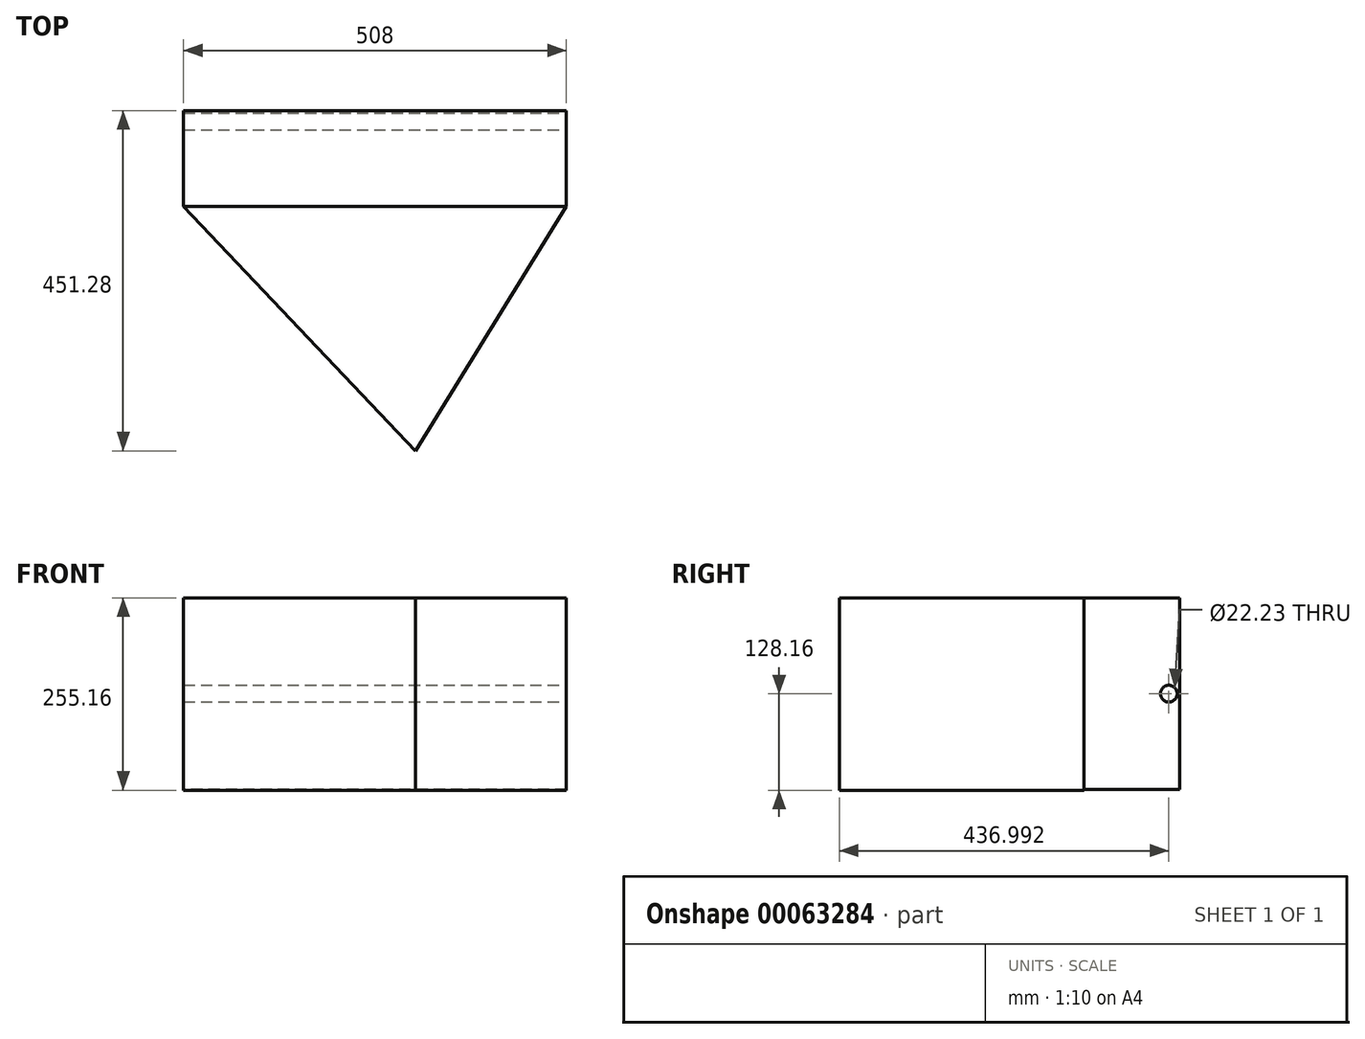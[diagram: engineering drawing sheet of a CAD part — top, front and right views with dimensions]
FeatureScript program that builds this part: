
annotation { "Feature Type Name" : "Feature", "Feature Type Description" : "" }
export const myFeature = defineFeature(function(context is Context, id is Id, definition is map)
    precondition{}
    {
        {
            var Q0;
            Q0=qCreatedBy(makeId("Front.planeOp"),FACE);
            var sketch = newSketch(context, id + "F0", { "sketchPlane" : qUnion([Q0])});
            skLineSegment(sketch, "E0.rect.bottom", {"start": v(254, 127) * mm, "end": v(-254, 127) * mm});
            skLineSegment(sketch, "E0.rect.top", {"start": v(254, -127) * mm, "end": v(-254, -127) * mm});
            skLineSegment(sketch, "E0.rect.left", {"start": v(254, 127) * mm, "end": v(254, -127) * mm});
            skLineSegment(sketch, "E0.rect.right", {"start": v(-254, 127) * mm, "end": v(-254, -127) * mm});
            skPoint(sketch, "E0.rect.middle", {"position": v(0, 0) * mm});
            skSolve(sketch);
        }
        {
            var Q0;
            Q0 = qSketchRegion(id + "F0", true);
            extrude(context, id + "F1", {"entities" : qUnion([Q0]), "depth" : 127 * mm});
        }
        {
            var Q0;
            Q0=makeQuery(id+"F1.opExtrude","SWEPT_FACE",FACE,{"disambiguationData":[OSD([sQuery(id+"F0.wireOp",EDGE,"E0.rect.bottom")])]});
            var sketch = newSketch(context, id + "F2", { "sketchPlane" : qUnion([Q0])});
            skLineSegment(sketch, "E1", {"start": v(254, -127) * mm, "end": v(54, -451.28) * mm});
            skLineSegment(sketch, "E2", {"start": v(54, -451.28) * mm, "end": v(-254, -127) * mm});
            skLineSegment(sketch, "E3", {"start": v(-254, -127) * mm, "end": v(254, -127) * mm});
            skSolve(sketch);
        }
        {
            var Q0;
            Q0 = qSketchRegion(id + "F2", true);
            extrude(context, id + "F3", {"entities" : qUnion([Q0]), "oppositeDirection" : true, "depth" : 255.16 * mm});
        }
        {
            var Q0;
            Q0=makeQuery(id+"F1.opExtrude","SWEPT_FACE",FACE,{"disambiguationData":[OSD([sQuery(id+"F0.wireOp",EDGE,"E0.rect.right")])]});
            var sketch = newSketch(context, id + "F4", { "sketchPlane" : qUnion([Q0])});
            skCircle(sketch, "E4", {"center": v(23.77, 0) * mm, "radius": 25.4 * mm});
            skSolve(sketch);
        }
        {
            var Q0;
            Q0 = qSketchRegion(id + "F4", true);
            extrude(context, id + "F5", {"entities" : qUnion([Q0]), "operationType" : NewBodyOperationType.REMOVE, "depth" : 897.98 * mm});
        }
        {
            var Q0;
            Q0=makeQuery(id+"F1.opExtrude","SWEPT_FACE",FACE,{"disambiguationData":[OSD([sQuery(id+"F0.wireOp",EDGE,"E0.rect.left")])]});
            var sketch = newSketch(context, id + "F6", { "sketchPlane" : qUnion([Q0])});
            skCircle(sketch, "E5", {"center": v(-14.29, 0) * mm, "radius": 11.11 * mm});
            skSolve(sketch);
        }
        {
            var Q0;
            Q0 = qSketchRegion(id + "F6", true);
            extrude(context, id + "F7", {"entities" : qUnion([Q0]), "operationType" : NewBodyOperationType.REMOVE, "oppositeDirection" : true, "depth" : 986.38 * mm});
        }
    });
